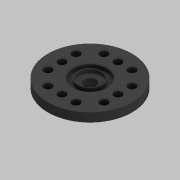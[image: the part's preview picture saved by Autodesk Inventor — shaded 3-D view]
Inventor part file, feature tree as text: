
AUTODESK INVENTOR PART (.ipt)
format: ipt  version: 2021 (Build 250183000, 183)  size: 168,448 bytes
history: native  units: mm
features: extrude x4, sketch x4, other x1, pattern_circular x1
ambient origin geometry x8: Origin, YZ Plane, XZ Plane, XY Plane, X Axis, Y Axis, Z Axis, Center Point
bodies: Body1 (feature_tree)
feature tree (10):
  other  "솔리드1"
  extrude  "돌출1"  Depth=8.7mm
  extrude  "돌출2"  Depth=5.5mm
  extrude  "돌출3"  Depth=3.0mm TaperAngle=0.0deg
  extrude  "돌출4"  Depth=21.0mm
  pattern_circular  "원형 패턴1"  [2 undecoded]
  sketch  "스케치1"
  sketch  "스케치3"
  sketch  "스케치4"
  sketch  "스케치5"
note: 2 required parameter values undecoded (feature->parameter linkage not recoverable at this tier; creation-order binding heuristic only, values carry confidence <= 0.55)
